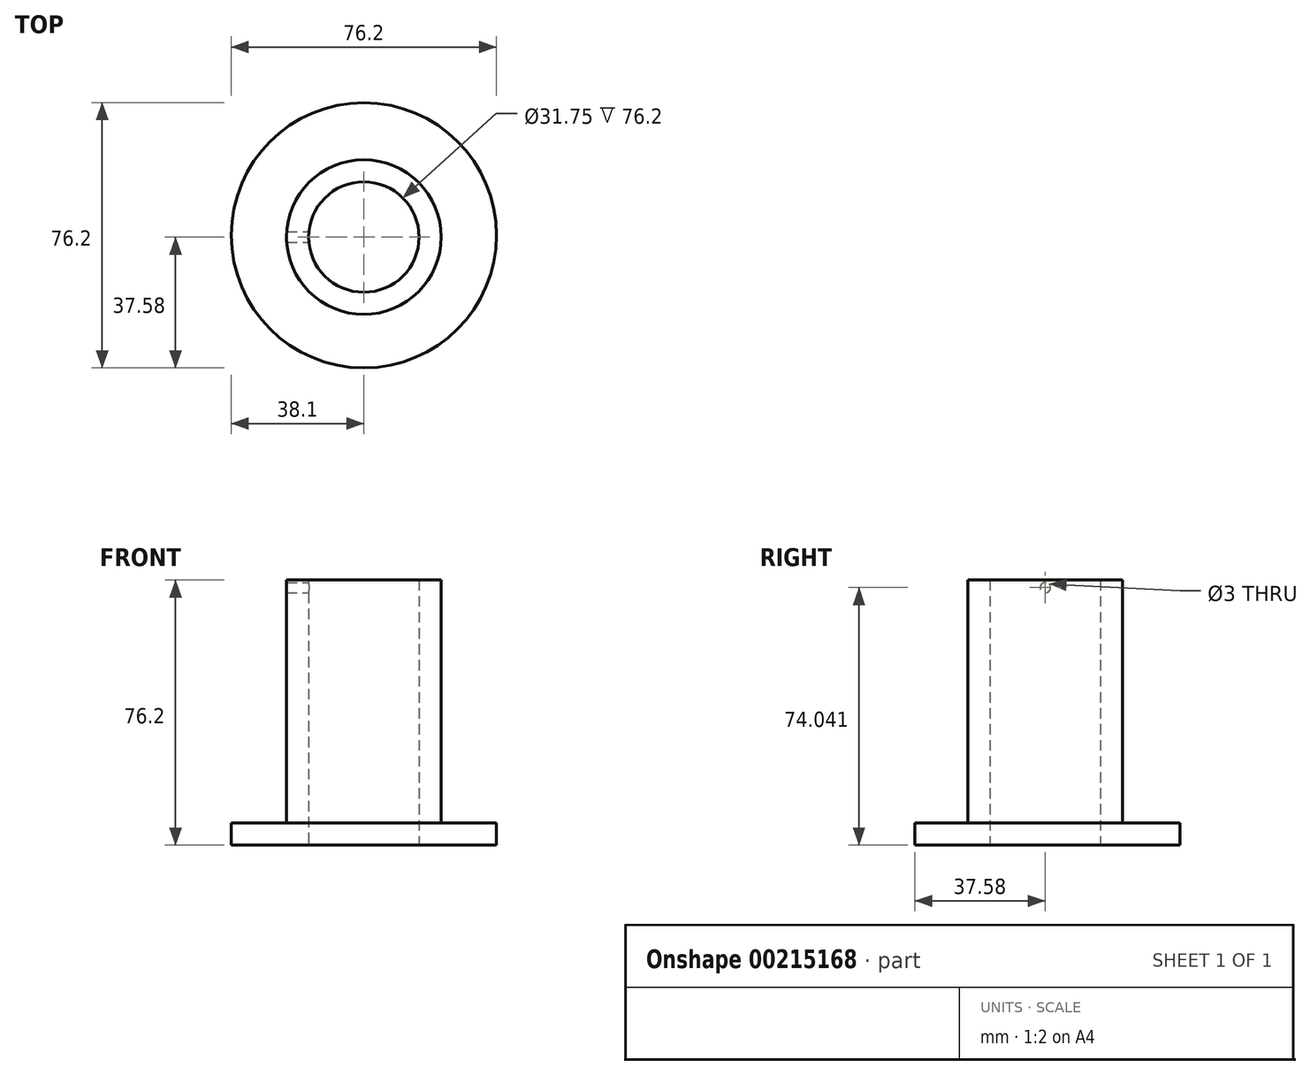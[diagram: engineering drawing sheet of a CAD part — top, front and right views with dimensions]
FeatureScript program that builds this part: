
annotation { "Feature Type Name" : "Feature", "Feature Type Description" : "" }
export const myFeature = defineFeature(function(context is Context, id is Id, definition is map)
    precondition{}
    {
        {
            var Q0;
            Q0=qCreatedBy(makeId("Top.planeOp"),FACE);
            var sketch = newSketch(context, id + "F0", { "sketchPlane" : qUnion([Q0])});
            skCircle(sketch, "E0", {"center": v(0, 0) * mm, "radius": 22.22 * mm});
            skCircle(sketch, "E1", {"center": v(0, 0) * mm, "radius": 15.88 * mm});
            skSolve(sketch);
        }
        {
            var Q0;
            Q0 = qSketchRegion(id + "F0", true);
            extrude(context, id + "F1", {"entities" : qUnion([Q0]), "depth" : 76.2 * mm});
        }
        {
            var Q0;
            Q0=qCreatedBy(makeId("Right.planeOp"),FACE);
            var sketch = newSketch(context, id + "F2", { "sketchPlane" : qUnion([Q0])});
            skCircle(sketch, "E2", {"center": v(0, 74.04) * mm, "radius": 1.5 * mm});
            skSolve(sketch);
        }
        {
            var Q0;
            Q0 = qSketchRegion(id + "F2", true);
            extrude(context, id + "F3", {"entities" : qUnion([Q0]), "operationType" : NewBodyOperationType.REMOVE, "oppositeDirection" : true, "depth" : 25 * mm});
        }
        {
            var Q0;
            Q0=makeQuery(id+"F1.opExtrude","CAP_FACE",FACE,{"disambiguationData":[OSD([sQuery(id+"F0.wireOp",EDGE,"E0"),sQuery(id+"F0.wireOp",EDGE,"E1")])],"isStart":true});
            var sketch = newSketch(context, id + "F4", { "sketchPlane" : qUnion([Q0])});
            skCircle(sketch, "E3.0", {"center": v(0, 0) * mm, "radius": 22.22 * mm});
            skCircle(sketch, "E4", {"center": v(0, -0.52) * mm, "radius": 38.1 * mm});
            skSolve(sketch);
        }
        {
            var Q0;
            Q0 = qSketchRegion(id + "F4", true);
            extrude(context, id + "F5", {"entities" : qUnion([Q0]), "operationType" : NewBodyOperationType.ADD, "oppositeDirection" : true, "depth" : 6.35 * mm});
        }
    });
